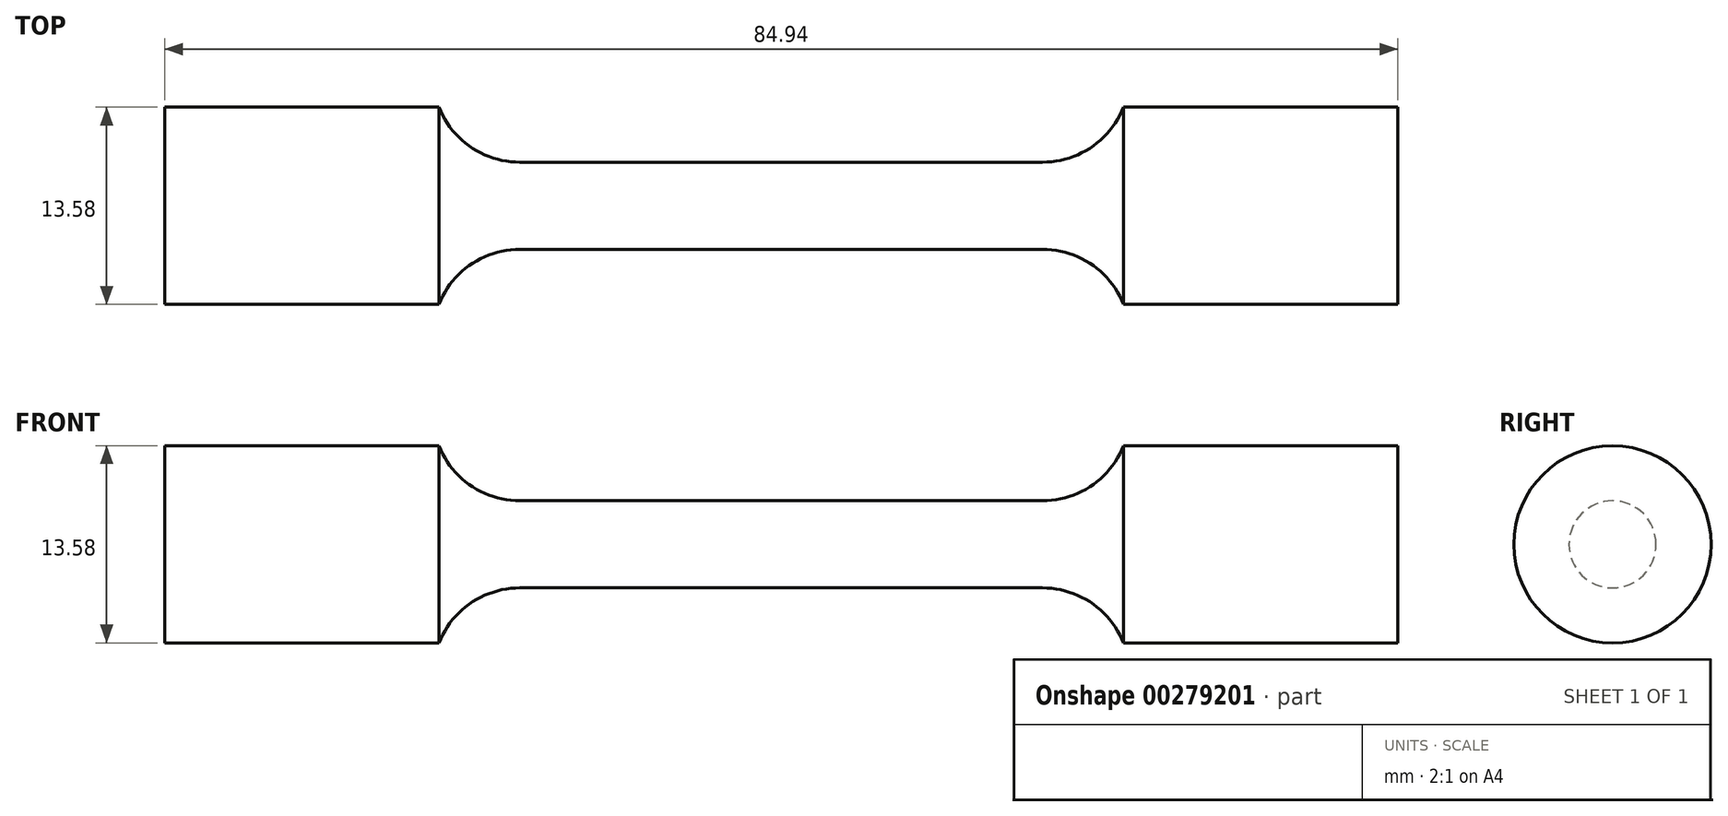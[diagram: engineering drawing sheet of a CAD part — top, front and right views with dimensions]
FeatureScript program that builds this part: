
annotation { "Feature Type Name" : "Feature", "Feature Type Description" : "" }
export const myFeature = defineFeature(function(context is Context, id is Id, definition is map)
    precondition{}
    {
        {
            var Q0;
            Q0=qCreatedBy(makeId("Front.planeOp"),FACE);
            var sketch = newSketch(context, id + "F0", { "sketchPlane" : qUnion([Q0])});
            skLineSegment(sketch, "E0", {"start": v(0, 3) * mm, "end": v(18, 3) * mm});
            skArc(sketch, "E1", {"start": v(18, 3) * mm, "mid": v(21.37, 4.04) * mm, "end": v(23.58, 6.8) * mm});
            skLineSegment(sketch, "E2", {"start": v(23.58, 6.8) * mm, "end": v(42.47, 6.8) * mm});
            skLineSegment(sketch, "E3", {"start": v(42.47, 0) * mm, "end": v(42.47, 6.8) * mm});
            skLineSegment(sketch, "E4.MirrorCS", {"start": v(0, 3) * mm, "end": v(-18, 3) * mm});
            skLineSegment(sketch, "E5.MirrorCS", {"start": v(-42.47, 0) * mm, "end": v(-42.47, 6.8) * mm});
            skLineSegment(sketch, "E6.MirrorCS", {"start": v(-23.58, 6.8) * mm, "end": v(-42.47, 6.8) * mm});
            skArc(sketch, "E7.MirrorCS", {"start": v(-18, 3) * mm, "mid": v(-21.37, 4.04) * mm, "end": v(-23.58, 6.8) * mm});
            skLineSegment(sketch, "E8", {"start": v(-42.47, 0) * mm, "end": v(42.47, 0) * mm});
            skSolve(sketch);
        }
        {
            var Q0;
            Q0=makeQuery(id+"F0.imprint","IMPRINT",FACE,{"disambiguationData":[TD([[makeQuery(id+"F0.imprint","IMPRINT",EDGE,{"derivedFrom":sQuery(id+"F0.wireOp",EDGE,"E0")}),-1.0]])]});
            var Q1;
            Q1=sQuery(id+"F0.wireOp",EDGE,"E8");
            revolve(context, id + "F1", {"entities" : qUnion([Q0]), "axis" : qUnion([Q1]), "revolveType" : RevolveType.FULL});
        }
    });
